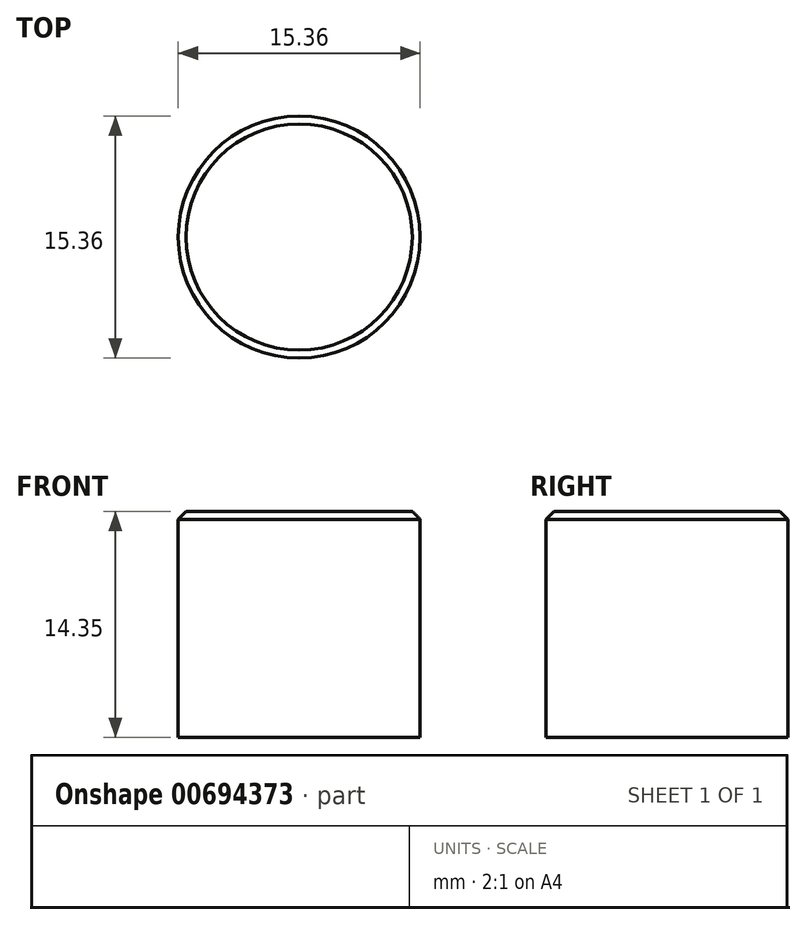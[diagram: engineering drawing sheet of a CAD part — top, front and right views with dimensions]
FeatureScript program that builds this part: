
annotation { "Feature Type Name" : "Feature", "Feature Type Description" : "" }
export const myFeature = defineFeature(function(context is Context, id is Id, definition is map)
    precondition{}
    {
        {
            var Q0;
            Q0=qCreatedBy(makeId("Top.planeOp"),FACE);
            var sketch = newSketch(context, id + "F0", { "sketchPlane" : qUnion([Q0])});
            skCircle(sketch, "E0", {"center": v(0, 0) * mm, "radius": 7.68 * mm});
            skSolve(sketch);
        }
        {
            var Q0;
            Q0=makeQuery(id+"F0.imprint","IMPRINT",FACE,{"disambiguationData":[TD([[makeQuery(id+"F0.imprint","IMPRINT",EDGE,{"derivedFrom":sQuery(id+"F0.wireOp",EDGE,"E0")}),1.0]])]});
            extrude(context, id + "F1", {"entities" : qUnion([Q0]), "depth" : ((.415 + .150) * 25.4) * mm, "offsetDistance" : 25 * mm});
        }
        {
            var Q0;
            Q0=qCreatedBy(makeId("Front.planeOp"),FACE);
            var sketch = newSketch(context, id + "F2", { "sketchPlane" : qUnion([Q0])});
            skFitSpline(sketch, "E1", {"points": [v(0, 15.93) * mm, v(3.3, 15.74) * mm, v(7.56, 14.35) * mm], "startDerivative": vector(6.93, 0.06) * mm, "endDerivative": vector(8.03, -2.97) * mm});
            skLineSegment(sketch, "E2", {"start": v(7.56, 14.61) * mm, "end": v(7.56, 13.9) * mm, "construction": true});
            skLineSegment(sketch, "E3", {"start": v(0, 16.51) * mm, "end": v(0, 14.76) * mm, "construction": true});
            skLineSegment(sketch, "E4", {"start": v(7.56, 14.35) * mm, "end": v(0, 14.35) * mm});
            skLineSegment(sketch, "E5", {"start": v(0, 14.35) * mm, "end": v(0, 15.93) * mm});
            skSolve(sketch);
        }
        {
            var Q0;
            Q0=qCreatedBy(makeId("Top.planeOp"),FACE);
            var sketch = newSketch(context, id + "F3", { "sketchPlane" : qUnion([Q0])});
            skLineSegment(sketch, "E6.bottom", {"start": v(0.35, 6.75) * mm, "end": v(-0.35, 6.75) * mm});
            skLineSegment(sketch, "E6.top", {"start": v(0.35, 7.75) * mm, "end": v(-0.35, 7.75) * mm});
            skLineSegment(sketch, "E6.left", {"start": v(0.35, 6.75) * mm, "end": v(0.35, 7.75) * mm});
            skLineSegment(sketch, "E6.right", {"start": v(-0.35, 6.75) * mm, "end": v(-0.35, 7.75) * mm});
            skPoint(sketch, "E6.middle", {"position": v(0, 7.25) * mm});
            skLineSegment(sketch, "E7.1.0", {"start": v(-1.27, 7.65) * mm, "end": v(-1.95, 7.5) * mm});
            skLineSegment(sketch, "E7.1.1", {"start": v(-1.74, 6.53) * mm, "end": v(-1.95, 7.5) * mm});
            skLineSegment(sketch, "E7.1.2", {"start": v(-1.06, 6.67) * mm, "end": v(-1.27, 7.65) * mm});
            skLineSegment(sketch, "E7.1.3", {"start": v(-1.06, 6.67) * mm, "end": v(-1.74, 6.53) * mm});
            skLineSegment(sketch, "E7.2.0", {"start": v(-2.84, 7.22) * mm, "end": v(-3.47, 6.94) * mm});
            skLineSegment(sketch, "E7.2.1", {"start": v(-3.06, 6.02) * mm, "end": v(-3.47, 6.94) * mm});
            skLineSegment(sketch, "E7.2.2", {"start": v(-2.43, 6.3) * mm, "end": v(-2.84, 7.22) * mm});
            skLineSegment(sketch, "E7.2.3", {"start": v(-2.43, 6.3) * mm, "end": v(-3.06, 6.02) * mm});
            skLineSegment(sketch, "E7.3.0", {"start": v(-4.27, 6.47) * mm, "end": v(-4.83, 6.06) * mm});
            skLineSegment(sketch, "E7.3.1", {"start": v(-4.25, 5.26) * mm, "end": v(-4.83, 6.06) * mm});
            skLineSegment(sketch, "E7.3.2", {"start": v(-3.69, 5.66) * mm, "end": v(-4.27, 6.47) * mm});
            skLineSegment(sketch, "E7.3.3", {"start": v(-3.69, 5.66) * mm, "end": v(-4.25, 5.26) * mm});
            skLineSegment(sketch, "E7.4.0", {"start": v(-5.53, 5.44) * mm, "end": v(-5.99, 4.93) * mm});
            skLineSegment(sketch, "E7.4.1", {"start": v(-5.25, 4.26) * mm, "end": v(-5.99, 4.93) * mm});
            skLineSegment(sketch, "E7.4.2", {"start": v(-4.78, 4.77) * mm, "end": v(-5.53, 5.44) * mm});
            skLineSegment(sketch, "E7.4.3", {"start": v(-4.78, 4.77) * mm, "end": v(-5.25, 4.26) * mm});
            skLineSegment(sketch, "E7.5.0", {"start": v(-6.54, 4.17) * mm, "end": v(-6.88, 3.57) * mm});
            skLineSegment(sketch, "E7.5.1", {"start": v(-6.02, 3.07) * mm, "end": v(-6.88, 3.57) * mm});
            skLineSegment(sketch, "E7.5.2", {"start": v(-5.67, 3.67) * mm, "end": v(-6.54, 4.17) * mm});
            skLineSegment(sketch, "E7.5.3", {"start": v(-5.67, 3.67) * mm, "end": v(-6.02, 3.07) * mm});
            skLineSegment(sketch, "E7.6.0", {"start": v(-7.26, 2.72) * mm, "end": v(-7.48, 2.07) * mm});
            skLineSegment(sketch, "E7.6.1", {"start": v(-6.52, 1.76) * mm, "end": v(-7.48, 2.07) * mm});
            skLineSegment(sketch, "E7.6.2", {"start": v(-6.31, 2.41) * mm, "end": v(-7.26, 2.72) * mm});
            skLineSegment(sketch, "E7.6.3", {"start": v(-6.31, 2.41) * mm, "end": v(-6.52, 1.76) * mm});
            skLineSegment(sketch, "E7.7.0", {"start": v(-7.67, 1.15) * mm, "end": v(-7.74, 0.47) * mm});
            skLineSegment(sketch, "E7.7.1", {"start": v(-6.75, 0.36) * mm, "end": v(-7.74, 0.47) * mm});
            skLineSegment(sketch, "E7.7.2", {"start": v(-6.67, 1.05) * mm, "end": v(-7.67, 1.15) * mm});
            skLineSegment(sketch, "E7.7.3", {"start": v(-6.67, 1.05) * mm, "end": v(-6.75, 0.36) * mm});
            skLineSegment(sketch, "E7.8.0", {"start": v(-7.74, -0.47) * mm, "end": v(-7.67, -1.15) * mm});
            skLineSegment(sketch, "E7.8.1", {"start": v(-6.67, -1.05) * mm, "end": v(-7.67, -1.15) * mm});
            skLineSegment(sketch, "E7.8.2", {"start": v(-6.75, -0.36) * mm, "end": v(-7.74, -0.47) * mm});
            skLineSegment(sketch, "E7.8.3", {"start": v(-6.75, -0.36) * mm, "end": v(-6.67, -1.05) * mm});
            skLineSegment(sketch, "E7.9.0", {"start": v(-7.48, -2.07) * mm, "end": v(-7.26, -2.72) * mm});
            skLineSegment(sketch, "E7.9.1", {"start": v(-6.31, -2.41) * mm, "end": v(-7.26, -2.72) * mm});
            skLineSegment(sketch, "E7.9.2", {"start": v(-6.52, -1.76) * mm, "end": v(-7.48, -2.07) * mm});
            skLineSegment(sketch, "E7.9.3", {"start": v(-6.52, -1.76) * mm, "end": v(-6.31, -2.41) * mm});
            skLineSegment(sketch, "E7.10.0", {"start": v(-6.88, -3.57) * mm, "end": v(-6.54, -4.17) * mm});
            skLineSegment(sketch, "E7.10.1", {"start": v(-5.67, -3.67) * mm, "end": v(-6.54, -4.17) * mm});
            skLineSegment(sketch, "E7.10.2", {"start": v(-6.02, -3.07) * mm, "end": v(-6.88, -3.57) * mm});
            skLineSegment(sketch, "E7.10.3", {"start": v(-6.02, -3.07) * mm, "end": v(-5.67, -3.67) * mm});
            skLineSegment(sketch, "E7.11.0", {"start": v(-5.99, -4.93) * mm, "end": v(-5.53, -5.44) * mm});
            skLineSegment(sketch, "E7.11.1", {"start": v(-4.78, -4.77) * mm, "end": v(-5.53, -5.44) * mm});
            skLineSegment(sketch, "E7.11.2", {"start": v(-5.25, -4.26) * mm, "end": v(-5.99, -4.93) * mm});
            skLineSegment(sketch, "E7.11.3", {"start": v(-5.25, -4.26) * mm, "end": v(-4.78, -4.77) * mm});
            skLineSegment(sketch, "E7.12.0", {"start": v(-4.83, -6.06) * mm, "end": v(-4.27, -6.47) * mm});
            skLineSegment(sketch, "E7.12.1", {"start": v(-3.69, -5.66) * mm, "end": v(-4.27, -6.47) * mm});
            skLineSegment(sketch, "E7.12.2", {"start": v(-4.25, -5.26) * mm, "end": v(-4.83, -6.06) * mm});
            skLineSegment(sketch, "E7.12.3", {"start": v(-4.25, -5.26) * mm, "end": v(-3.69, -5.66) * mm});
            skLineSegment(sketch, "E7.13.0", {"start": v(-3.47, -6.94) * mm, "end": v(-2.84, -7.22) * mm});
            skLineSegment(sketch, "E7.13.1", {"start": v(-2.43, -6.3) * mm, "end": v(-2.84, -7.22) * mm});
            skLineSegment(sketch, "E7.13.2", {"start": v(-3.06, -6.02) * mm, "end": v(-3.47, -6.94) * mm});
            skLineSegment(sketch, "E7.13.3", {"start": v(-3.06, -6.02) * mm, "end": v(-2.43, -6.3) * mm});
            skLineSegment(sketch, "E7.14.0", {"start": v(-1.95, -7.5) * mm, "end": v(-1.27, -7.65) * mm});
            skLineSegment(sketch, "E7.14.1", {"start": v(-1.06, -6.67) * mm, "end": v(-1.27, -7.65) * mm});
            skLineSegment(sketch, "E7.14.2", {"start": v(-1.74, -6.53) * mm, "end": v(-1.95, -7.5) * mm});
            skLineSegment(sketch, "E7.14.3", {"start": v(-1.74, -6.53) * mm, "end": v(-1.06, -6.67) * mm});
            skLineSegment(sketch, "E7.15.0", {"start": v(-0.35, -7.75) * mm, "end": v(0.35, -7.75) * mm});
            skLineSegment(sketch, "E7.15.1", {"start": v(0.35, -6.75) * mm, "end": v(0.35, -7.75) * mm});
            skLineSegment(sketch, "E7.15.2", {"start": v(-0.35, -6.75) * mm, "end": v(-0.35, -7.75) * mm});
            skLineSegment(sketch, "E7.15.3", {"start": v(-0.35, -6.75) * mm, "end": v(0.35, -6.75) * mm});
            skLineSegment(sketch, "E7.16.0", {"start": v(1.27, -7.65) * mm, "end": v(1.95, -7.5) * mm});
            skLineSegment(sketch, "E7.16.1", {"start": v(1.74, -6.53) * mm, "end": v(1.95, -7.5) * mm});
            skLineSegment(sketch, "E7.16.2", {"start": v(1.06, -6.67) * mm, "end": v(1.27, -7.65) * mm});
            skLineSegment(sketch, "E7.16.3", {"start": v(1.06, -6.67) * mm, "end": v(1.74, -6.53) * mm});
            skLineSegment(sketch, "E7.17.0", {"start": v(2.84, -7.22) * mm, "end": v(3.47, -6.94) * mm});
            skLineSegment(sketch, "E7.17.1", {"start": v(3.06, -6.02) * mm, "end": v(3.47, -6.94) * mm});
            skLineSegment(sketch, "E7.17.2", {"start": v(2.43, -6.3) * mm, "end": v(2.84, -7.22) * mm});
            skLineSegment(sketch, "E7.17.3", {"start": v(2.43, -6.3) * mm, "end": v(3.06, -6.02) * mm});
            skLineSegment(sketch, "E7.18.0", {"start": v(4.27, -6.47) * mm, "end": v(4.83, -6.06) * mm});
            skLineSegment(sketch, "E7.18.1", {"start": v(4.25, -5.26) * mm, "end": v(4.83, -6.06) * mm});
            skLineSegment(sketch, "E7.18.2", {"start": v(3.69, -5.66) * mm, "end": v(4.27, -6.47) * mm});
            skLineSegment(sketch, "E7.18.3", {"start": v(3.69, -5.66) * mm, "end": v(4.25, -5.26) * mm});
            skLineSegment(sketch, "E7.19.0", {"start": v(5.53, -5.44) * mm, "end": v(5.99, -4.93) * mm});
            skLineSegment(sketch, "E7.19.1", {"start": v(5.25, -4.26) * mm, "end": v(5.99, -4.93) * mm});
            skLineSegment(sketch, "E7.19.2", {"start": v(4.78, -4.77) * mm, "end": v(5.53, -5.44) * mm});
            skLineSegment(sketch, "E7.19.3", {"start": v(4.78, -4.77) * mm, "end": v(5.25, -4.26) * mm});
            skLineSegment(sketch, "E7.20.0", {"start": v(6.54, -4.17) * mm, "end": v(6.88, -3.57) * mm});
            skLineSegment(sketch, "E7.20.1", {"start": v(6.02, -3.07) * mm, "end": v(6.88, -3.57) * mm});
            skLineSegment(sketch, "E7.20.2", {"start": v(5.67, -3.67) * mm, "end": v(6.54, -4.17) * mm});
            skLineSegment(sketch, "E7.20.3", {"start": v(5.67, -3.67) * mm, "end": v(6.02, -3.07) * mm});
            skLineSegment(sketch, "E7.21.0", {"start": v(7.26, -2.72) * mm, "end": v(7.48, -2.07) * mm});
            skLineSegment(sketch, "E7.21.1", {"start": v(6.52, -1.76) * mm, "end": v(7.48, -2.07) * mm});
            skLineSegment(sketch, "E7.21.2", {"start": v(6.31, -2.41) * mm, "end": v(7.26, -2.72) * mm});
            skLineSegment(sketch, "E7.21.3", {"start": v(6.31, -2.41) * mm, "end": v(6.52, -1.76) * mm});
            skLineSegment(sketch, "E7.22.0", {"start": v(7.67, -1.15) * mm, "end": v(7.74, -0.47) * mm});
            skLineSegment(sketch, "E7.22.1", {"start": v(6.75, -0.36) * mm, "end": v(7.74, -0.47) * mm});
            skLineSegment(sketch, "E7.22.2", {"start": v(6.67, -1.05) * mm, "end": v(7.67, -1.15) * mm});
            skLineSegment(sketch, "E7.22.3", {"start": v(6.67, -1.05) * mm, "end": v(6.75, -0.36) * mm});
            skLineSegment(sketch, "E7.23.0", {"start": v(7.74, 0.47) * mm, "end": v(7.67, 1.15) * mm});
            skLineSegment(sketch, "E7.23.1", {"start": v(6.67, 1.05) * mm, "end": v(7.67, 1.15) * mm});
            skLineSegment(sketch, "E7.23.2", {"start": v(6.75, 0.36) * mm, "end": v(7.74, 0.47) * mm});
            skLineSegment(sketch, "E7.23.3", {"start": v(6.75, 0.36) * mm, "end": v(6.67, 1.05) * mm});
            skLineSegment(sketch, "E7.24.0", {"start": v(7.48, 2.07) * mm, "end": v(7.26, 2.72) * mm});
            skLineSegment(sketch, "E7.24.1", {"start": v(6.31, 2.41) * mm, "end": v(7.26, 2.72) * mm});
            skLineSegment(sketch, "E7.24.2", {"start": v(6.52, 1.76) * mm, "end": v(7.48, 2.07) * mm});
            skLineSegment(sketch, "E7.24.3", {"start": v(6.52, 1.76) * mm, "end": v(6.31, 2.41) * mm});
            skLineSegment(sketch, "E7.25.0", {"start": v(6.88, 3.57) * mm, "end": v(6.54, 4.17) * mm});
            skLineSegment(sketch, "E7.25.1", {"start": v(5.67, 3.67) * mm, "end": v(6.54, 4.17) * mm});
            skLineSegment(sketch, "E7.25.2", {"start": v(6.02, 3.07) * mm, "end": v(6.88, 3.57) * mm});
            skLineSegment(sketch, "E7.25.3", {"start": v(6.02, 3.07) * mm, "end": v(5.67, 3.67) * mm});
            skLineSegment(sketch, "E7.26.0", {"start": v(5.99, 4.93) * mm, "end": v(5.53, 5.44) * mm});
            skLineSegment(sketch, "E7.26.1", {"start": v(4.78, 4.77) * mm, "end": v(5.53, 5.44) * mm});
            skLineSegment(sketch, "E7.26.2", {"start": v(5.25, 4.26) * mm, "end": v(5.99, 4.93) * mm});
            skLineSegment(sketch, "E7.26.3", {"start": v(5.25, 4.26) * mm, "end": v(4.78, 4.77) * mm});
            skLineSegment(sketch, "E7.27.0", {"start": v(4.83, 6.06) * mm, "end": v(4.27, 6.47) * mm});
            skLineSegment(sketch, "E7.27.1", {"start": v(3.69, 5.66) * mm, "end": v(4.27, 6.47) * mm});
            skLineSegment(sketch, "E7.27.2", {"start": v(4.25, 5.26) * mm, "end": v(4.83, 6.06) * mm});
            skLineSegment(sketch, "E7.27.3", {"start": v(4.25, 5.26) * mm, "end": v(3.69, 5.66) * mm});
            skLineSegment(sketch, "E7.28.0", {"start": v(3.47, 6.94) * mm, "end": v(2.84, 7.22) * mm});
            skLineSegment(sketch, "E7.28.1", {"start": v(2.43, 6.3) * mm, "end": v(2.84, 7.22) * mm});
            skLineSegment(sketch, "E7.28.2", {"start": v(3.06, 6.02) * mm, "end": v(3.47, 6.94) * mm});
            skLineSegment(sketch, "E7.28.3", {"start": v(3.06, 6.02) * mm, "end": v(2.43, 6.3) * mm});
            skLineSegment(sketch, "E7.29.0", {"start": v(1.95, 7.5) * mm, "end": v(1.27, 7.65) * mm});
            skLineSegment(sketch, "E7.29.1", {"start": v(1.06, 6.67) * mm, "end": v(1.27, 7.65) * mm});
            skLineSegment(sketch, "E7.29.2", {"start": v(1.74, 6.53) * mm, "end": v(1.95, 7.5) * mm});
            skLineSegment(sketch, "E7.29.3", {"start": v(1.74, 6.53) * mm, "end": v(1.06, 6.67) * mm});
            skPoint(sketch, "E7.center", {"position": v(0, 0) * mm});
            skSolve(sketch);
        }
        {
            var Q0;
            Q0=makeQuery(id+"F1.opExtrude","CAP_EDGE",EDGE,{"disambiguationData":[OSD([sQuery(id+"F0.wireOp",EDGE,"E0")])],"isStart":false});
            chamfer(context, id + "F4", {"entities" : qUnion([Q0]), "width" : 0.5 * mm, "tangentPropagation" : true});
        }
    });
